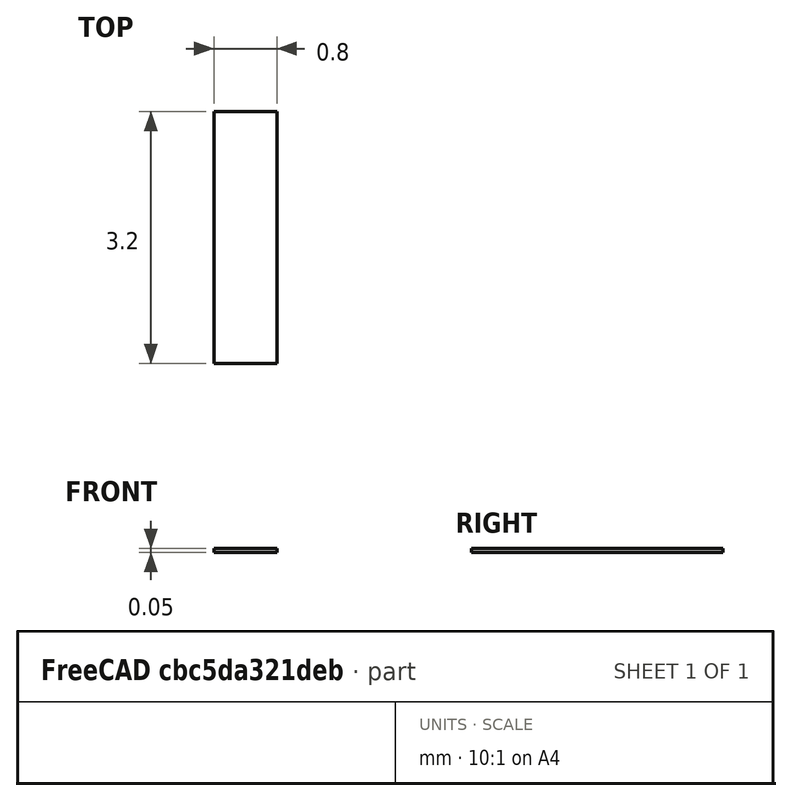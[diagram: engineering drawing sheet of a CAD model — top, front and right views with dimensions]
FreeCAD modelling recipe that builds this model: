
FCSTD DOCUMENT  (FreeCAD 0.17R12607 (Git))
Label: MicroSD Card Long Pin
License: All rights reserved
LicenseURL: http://en.wikipedia.org/wiki/All_rights_reserved
objects: Sketcher::SketchObject×1, PartDesign::Pad×1, PartDesign::Body×1
note: 4 computed .brp shape members not serialized (recipe doc carries the construction recipe); baked Part::Feature solids carry a one-line shape summary decoded from their .brp

FEATURE [Sketcher::SketchObject] Sketch  label="Pin Sketch"
  MapMode = 5
  Support = -> [XY_Plane]
  sketch-geometry (4):
    g0: LineSegment StartX=-0.4 StartY=-1.6 StartZ=0 EndX=0.4 EndY=-1.6 EndZ=0
    g1: LineSegment StartX=0.4 StartY=-1.6 StartZ=0 EndX=0.4 EndY=1.6 EndZ=0
    g2: LineSegment StartX=0.4 StartY=1.6 StartZ=0 EndX=-0.4 EndY=1.6 EndZ=0
    g3: LineSegment StartX=-0.4 StartY=1.6 StartZ=0 EndX=-0.4 EndY=-1.6 EndZ=0
  constraints (12):
    c: Coincident(g0,g1)
    c: Coincident(g1,g2)
    c: Coincident(g2,g3)
    c: Coincident(g3,g0)
    c: Horizontal(g0)
    c: Horizontal(g2)
    c: Vertical(g1)
    c: Vertical(g3)
    c: DistanceX(g2,g2) = 0.8
    c: DistanceY(g1,g1) = 3.2
    c: Symmetric(g2,g1,g-2)
    c: Symmetric(g1,g0,g-1)
FEATURE [PartDesign::Pad] Pad  label="Pin"
  Length = 0.05
  Length2 = 100
  Profile = -> Sketch
  Type = 0
FEATURE [PartDesign::Body] Body
  Group = -> [Sketch,Pad]
  Origin = -> Origin
  Tip = -> Pad
